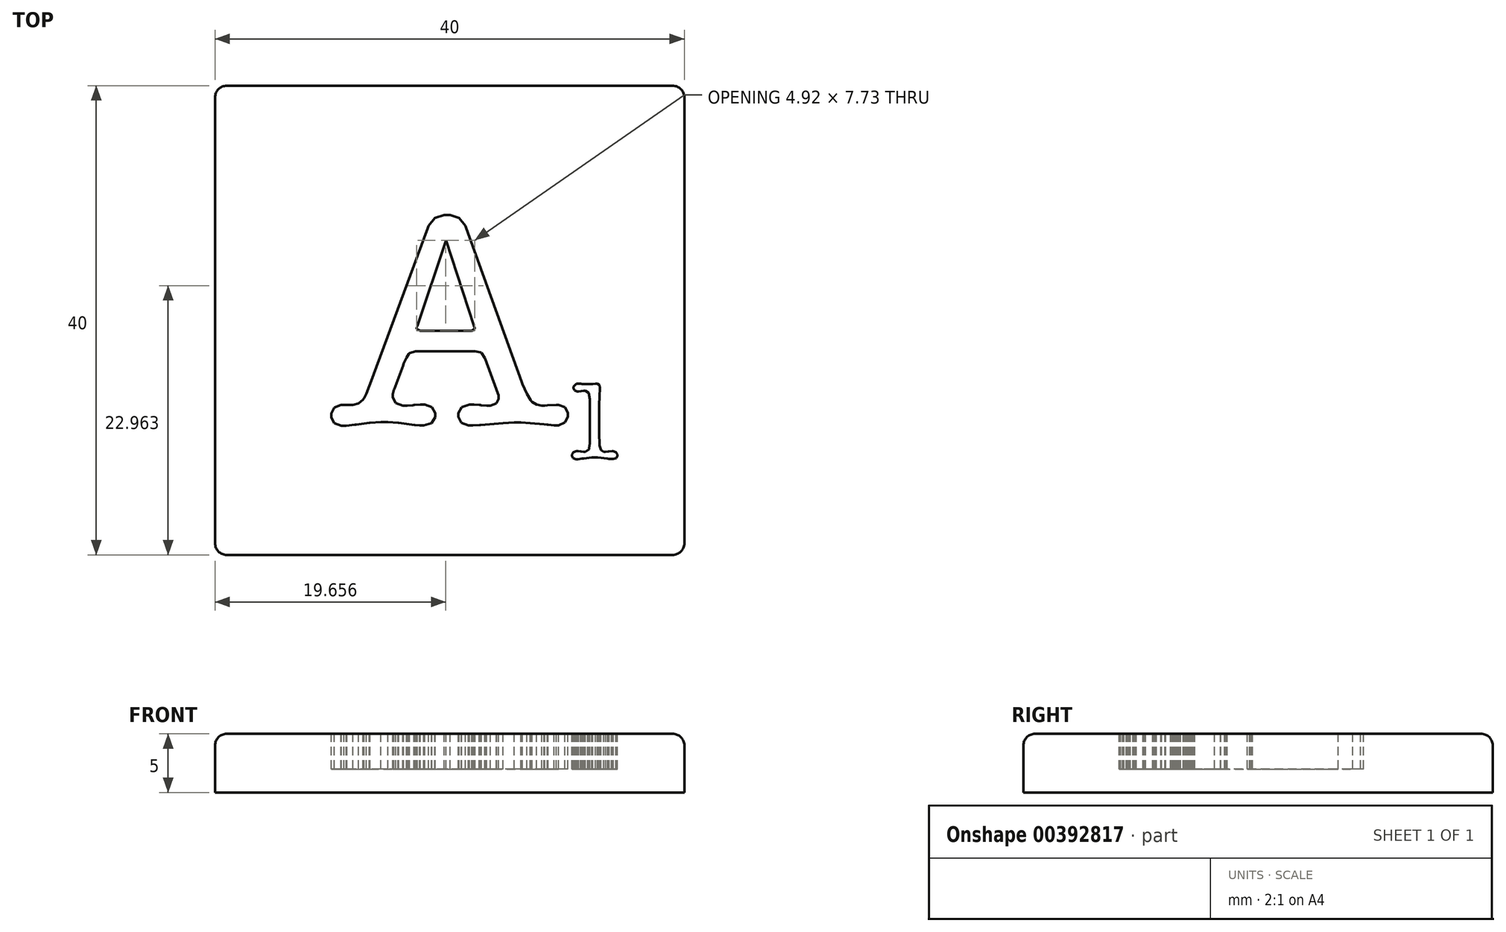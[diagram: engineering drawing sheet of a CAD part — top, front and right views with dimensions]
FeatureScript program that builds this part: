
annotation { "Feature Type Name" : "Feature", "Feature Type Description" : "" }
export const myFeature = defineFeature(function(context is Context, id is Id, definition is map)
    precondition{}
    {
        {
            var Q0;
            Q0=qCreatedBy(makeId("Top.planeOp"),FACE);
            var sketch = newSketch(context, id + "F0", { "sketchPlane" : qUnion([Q0])});
            skLineSegment(sketch, "E0.bottom", {"start": v(20, -20) * mm, "end": v(-20, -20) * mm});
            skLineSegment(sketch, "E0.top", {"start": v(20, 20) * mm, "end": v(-20, 20) * mm});
            skLineSegment(sketch, "E0.left", {"start": v(20, -20) * mm, "end": v(20, 20) * mm});
            skLineSegment(sketch, "E0.right", {"start": v(-20, -20) * mm, "end": v(-20, 20) * mm});
            skPoint(sketch, "E0.middle", {"position": v(0, 0) * mm});
            skSolve(sketch);
        }
        {
            var Q0;
            Q0=makeQuery(id+"F0.imprint","IMPRINT",FACE,{"disambiguationData":[TD([[makeQuery(id+"F0.imprint","IMPRINT",EDGE,{"derivedFrom":sQuery(id+"F0.wireOp",EDGE,"E0.bottom")}),-1.0]])]});
            extrude(context, id + "F1", {"entities" : qUnion([Q0]), "depth" : -5 * mm});
        }
        {
            var Q0;
            Q0=makeQuery(id+"F1.opExtrude","CAP_FACE",FACE,{"disambiguationData":[OSD([sQuery(id+"F0.wireOp",EDGE,"E0.bottom"),sQuery(id+"F0.wireOp",EDGE,"E0.top"),sQuery(id+"F0.wireOp",EDGE,"E0.left"),sQuery(id+"F0.wireOp",EDGE,"E0.right")])],"isStart":true});
            var Q1;
            Q1=makeQuery(id+"F1.opExtrude","SWEPT_EDGE",EDGE,{"disambiguationData":[OSD([sQuery(id+"F0.wireOp",EDGE,"E0.top"),sQuery(id+"F0.wireOp",EDGE,"E0.right")])]});
            var Q2;
            Q2=makeQuery(id+"F1.opExtrude","SWEPT_EDGE",EDGE,{"disambiguationData":[OSD([sQuery(id+"F0.wireOp",EDGE,"E0.top"),sQuery(id+"F0.wireOp",EDGE,"E0.left")])]});
            var Q3;
            Q3=makeQuery(id+"F1.opExtrude","SWEPT_EDGE",EDGE,{"disambiguationData":[OSD([sQuery(id+"F0.wireOp",EDGE,"E0.bottom"),sQuery(id+"F0.wireOp",EDGE,"E0.right")])]});
            var Q4;
            Q4=makeQuery(id+"F1.opExtrude","SWEPT_EDGE",EDGE,{"disambiguationData":[OSD([sQuery(id+"F0.wireOp",EDGE,"E0.bottom"),sQuery(id+"F0.wireOp",EDGE,"E0.left")])]});
            fillet(context, id + "F2", {"entities" : qUnion([Q0, Q1, Q2, Q3, Q4]), "radius" : 1 * mm, "tangentPropagation" : true, "allowEdgeOverflow" : false});
        }
        {
            var Q0;
            Q0=qCreatedBy(makeId("Top.planeOp"),FACE);
            var sketch = newSketch(context, id + "F3", { "sketchPlane" : qUnion([Q0])});
            skLineSegment(sketch, "E1", {"start": v(3.97, -5.87) * mm, "end": v(3.02, -3.28) * mm});
            skLineSegment(sketch, "E2", {"start": v(3.02, -3.28) * mm, "end": v(2.99, -3.2) * mm});
            skLineSegment(sketch, "E3", {"start": v(2.99, -3.2) * mm, "end": v(2.71, -2.77) * mm});
            skLineSegment(sketch, "E4", {"start": v(2.71, -2.77) * mm, "end": v(2.69, -2.75) * mm});
            skLineSegment(sketch, "E5", {"start": v(2.69, -2.75) * mm, "end": v(2.66, -2.73) * mm});
            skLineSegment(sketch, "E6", {"start": v(2.66, -2.73) * mm, "end": v(2.15, -2.65) * mm});
            skLineSegment(sketch, "E7", {"start": v(2.15, -2.65) * mm, "end": v(1.99, -2.65) * mm});
            skLineSegment(sketch, "E8", {"start": v(1.99, -2.65) * mm, "end": v(-2.73, -2.65) * mm});
            skLineSegment(sketch, "E9", {"start": v(-2.73, -2.65) * mm, "end": v(-2.9, -2.65) * mm});
            skLineSegment(sketch, "E10", {"start": v(-2.9, -2.65) * mm, "end": v(-3.42, -2.8) * mm});
            skLineSegment(sketch, "E11", {"start": v(-3.42, -2.8) * mm, "end": v(-3.45, -2.83) * mm});
            skLineSegment(sketch, "E12", {"start": v(-3.45, -2.83) * mm, "end": v(-3.49, -2.86) * mm});
            skLineSegment(sketch, "E13", {"start": v(-3.49, -2.86) * mm, "end": v(-3.68, -3.17) * mm});
            skLineSegment(sketch, "E14", {"start": v(-3.68, -3.17) * mm, "end": v(-3.92, -3.7) * mm});
            skLineSegment(sketch, "E15", {"start": v(-3.92, -3.7) * mm, "end": v(-3.97, -3.84) * mm});
            skLineSegment(sketch, "E16", {"start": v(-3.97, -3.84) * mm, "end": v(-4.74, -5.87) * mm});
            skLineSegment(sketch, "E17", {"start": v(-4.74, -5.87) * mm, "end": v(-4.75, -5.92) * mm});
            skLineSegment(sketch, "E18", {"start": v(-4.75, -5.92) * mm, "end": v(-4.84, -6.3) * mm});
            skLineSegment(sketch, "E19", {"start": v(-4.84, -6.3) * mm, "end": v(-4.84, -6.43) * mm});
            skLineSegment(sketch, "E20", {"start": v(-4.84, -6.43) * mm, "end": v(-4.84, -6.59) * mm});
            skLineSegment(sketch, "E21", {"start": v(-4.84, -6.59) * mm, "end": v(-4.58, -7.06) * mm});
            skLineSegment(sketch, "E22", {"start": v(-4.58, -7.06) * mm, "end": v(-4, -7.28) * mm});
            skLineSegment(sketch, "E23", {"start": v(-4, -7.28) * mm, "end": v(-3.8, -7.28) * mm});
            skLineSegment(sketch, "E24", {"start": v(-3.8, -7.28) * mm, "end": v(-3.62, -7.28) * mm});
            skLineSegment(sketch, "E25", {"start": v(-3.62, -7.28) * mm, "end": v(-3.14, -7.23) * mm});
            skLineSegment(sketch, "E26", {"start": v(-3.14, -7.23) * mm, "end": v(-3.06, -7.22) * mm});
            skLineSegment(sketch, "E27", {"start": v(-3.06, -7.22) * mm, "end": v(-2.97, -7.21) * mm});
            skLineSegment(sketch, "E28", {"start": v(-2.97, -7.21) * mm, "end": v(-2.5, -7.17) * mm});
            skLineSegment(sketch, "E29", {"start": v(-2.5, -7.17) * mm, "end": v(-2.33, -7.17) * mm});
            skLineSegment(sketch, "E30", {"start": v(-2.33, -7.17) * mm, "end": v(-2.13, -7.17) * mm});
            skLineSegment(sketch, "E31", {"start": v(-2.13, -7.17) * mm, "end": v(-1.52, -7.4) * mm});
            skLineSegment(sketch, "E32", {"start": v(-1.52, -7.4) * mm, "end": v(-1.24, -7.92) * mm});
            skLineSegment(sketch, "E33", {"start": v(-1.24, -7.92) * mm, "end": v(-1.24, -8.1) * mm});
            skLineSegment(sketch, "E34", {"start": v(-1.24, -8.1) * mm, "end": v(-1.24, -8.26) * mm});
            skLineSegment(sketch, "E35", {"start": v(-1.24, -8.26) * mm, "end": v(-1.54, -8.75) * mm});
            skLineSegment(sketch, "E36", {"start": v(-1.54, -8.75) * mm, "end": v(-2.21, -8.97) * mm});
            skLineSegment(sketch, "E37", {"start": v(-2.21, -8.97) * mm, "end": v(-2.43, -8.97) * mm});
            skLineSegment(sketch, "E38", {"start": v(-2.43, -8.97) * mm, "end": v(-2.58, -8.97) * mm});
            skLineSegment(sketch, "E39", {"start": v(-2.58, -8.97) * mm, "end": v(-2.96, -8.92) * mm});
            skLineSegment(sketch, "E40", {"start": v(-2.96, -8.92) * mm, "end": v(-3.02, -8.92) * mm});
            skLineSegment(sketch, "E41", {"start": v(-3.02, -8.92) * mm, "end": v(-4.34, -8.73) * mm});
            skLineSegment(sketch, "E42", {"start": v(-4.34, -8.73) * mm, "end": v(-4.4, -8.72) * mm});
            skLineSegment(sketch, "E43", {"start": v(-4.4, -8.72) * mm, "end": v(-5.27, -8.68) * mm});
            skLineSegment(sketch, "E44", {"start": v(-5.27, -8.68) * mm, "end": v(-5.56, -8.68) * mm});
            skLineSegment(sketch, "E45", {"start": v(-5.56, -8.68) * mm, "end": v(-5.88, -8.68) * mm});
            skLineSegment(sketch, "E46", {"start": v(-5.88, -8.68) * mm, "end": v(-6.8, -8.72) * mm});
            skLineSegment(sketch, "E47", {"start": v(-6.8, -8.72) * mm, "end": v(-6.85, -8.73) * mm});
            skLineSegment(sketch, "E48", {"start": v(-6.85, -8.73) * mm, "end": v(-7.96, -8.89) * mm});
            skLineSegment(sketch, "E49", {"start": v(-7.96, -8.89) * mm, "end": v(-8.09, -8.9) * mm});
            skLineSegment(sketch, "E50", {"start": v(-8.09, -8.9) * mm, "end": v(-8.8, -9) * mm});
            skLineSegment(sketch, "E51", {"start": v(-8.8, -9) * mm, "end": v(-9.05, -9) * mm});
            skLineSegment(sketch, "E52", {"start": v(-9.05, -9) * mm, "end": v(-9.24, -9) * mm});
            skLineSegment(sketch, "E53", {"start": v(-9.24, -9) * mm, "end": v(-9.82, -8.78) * mm});
            skLineSegment(sketch, "E54", {"start": v(-9.82, -8.78) * mm, "end": v(-10.08, -8.28) * mm});
            skLineSegment(sketch, "E55", {"start": v(-10.08, -8.28) * mm, "end": v(-10.08, -8.12) * mm});
            skLineSegment(sketch, "E56", {"start": v(-10.08, -8.12) * mm, "end": v(-10.08, -7.95) * mm});
            skLineSegment(sketch, "E57", {"start": v(-10.08, -7.95) * mm, "end": v(-9.83, -7.43) * mm});
            skLineSegment(sketch, "E58", {"start": v(-9.83, -7.43) * mm, "end": v(-9.26, -7.2) * mm});
            skLineSegment(sketch, "E59", {"start": v(-9.26, -7.2) * mm, "end": v(-9.08, -7.2) * mm});
            skLineSegment(sketch, "E60", {"start": v(-9.08, -7.2) * mm, "end": v(-9, -7.2) * mm});
            skLineSegment(sketch, "E61", {"start": v(-9, -7.2) * mm, "end": v(-8.78, -7.22) * mm});
            skLineSegment(sketch, "E62", {"start": v(-8.78, -7.22) * mm, "end": v(-8.76, -7.22) * mm});
            skLineSegment(sketch, "E63", {"start": v(-8.76, -7.22) * mm, "end": v(-8.41, -7.22) * mm});
            skLineSegment(sketch, "E64", {"start": v(-8.41, -7.22) * mm, "end": v(-8.26, -7.22) * mm});
            skLineSegment(sketch, "E65", {"start": v(-8.26, -7.22) * mm, "end": v(-7.79, -7.08) * mm});
            skLineSegment(sketch, "E66", {"start": v(-7.79, -7.08) * mm, "end": v(-7.4, -6.76) * mm});
            skLineSegment(sketch, "E67", {"start": v(-7.4, -6.76) * mm, "end": v(-7.33, -6.67) * mm});
            skLineSegment(sketch, "E68", {"start": v(-7.33, -6.67) * mm, "end": v(-7.3, -6.63) * mm});
            skLineSegment(sketch, "E69", {"start": v(-7.3, -6.63) * mm, "end": v(-7.12, -6.25) * mm});
            skLineSegment(sketch, "E70", {"start": v(-7.12, -6.25) * mm, "end": v(-6.86, -5.6) * mm});
            skLineSegment(sketch, "E71", {"start": v(-6.86, -5.6) * mm, "end": v(-6.8, -5.42) * mm});
            skLineSegment(sketch, "E72", {"start": v(-6.8, -5.42) * mm, "end": v(-1.88, 7.89) * mm});
            skLineSegment(sketch, "E73", {"start": v(-1.88, 7.89) * mm, "end": v(-1.8, 8.07) * mm});
            skLineSegment(sketch, "E74", {"start": v(-1.8, 8.07) * mm, "end": v(-1.25, 8.72) * mm});
            skLineSegment(sketch, "E75", {"start": v(-1.25, 8.72) * mm, "end": v(-0.47, 9) * mm});
            skLineSegment(sketch, "E76", {"start": v(-0.47, 9) * mm, "end": v(-0.21, 9) * mm});
            skLineSegment(sketch, "E77", {"start": v(-0.21, 9) * mm, "end": v(0.04, 9) * mm});
            skLineSegment(sketch, "E78", {"start": v(0.04, 9) * mm, "end": v(0.8, 8.72) * mm});
            skLineSegment(sketch, "E79", {"start": v(0.8, 8.72) * mm, "end": v(1.34, 8.07) * mm});
            skLineSegment(sketch, "E80", {"start": v(1.34, 8.07) * mm, "end": v(1.4, 7.89) * mm});
            skLineSegment(sketch, "E81", {"start": v(1.4, 7.89) * mm, "end": v(6.14, -5.24) * mm});
            skLineSegment(sketch, "E82", {"start": v(6.14, -5.24) * mm, "end": v(6.21, -5.45) * mm});
            skLineSegment(sketch, "E83", {"start": v(6.21, -5.45) * mm, "end": v(6.57, -6.27) * mm});
            skLineSegment(sketch, "E84", {"start": v(6.57, -6.27) * mm, "end": v(6.9, -6.81) * mm});
            skLineSegment(sketch, "E85", {"start": v(6.9, -6.81) * mm, "end": v(6.96, -6.88) * mm});
            skLineSegment(sketch, "E86", {"start": v(6.96, -6.88) * mm, "end": v(7.02, -6.95) * mm});
            skLineSegment(sketch, "E87", {"start": v(7.02, -6.95) * mm, "end": v(7.4, -7.18) * mm});
            skLineSegment(sketch, "E88", {"start": v(7.4, -7.18) * mm, "end": v(7.86, -7.28) * mm});
            skLineSegment(sketch, "E89", {"start": v(7.86, -7.28) * mm, "end": v(8.02, -7.28) * mm});
            skLineSegment(sketch, "E90", {"start": v(8.02, -7.28) * mm, "end": v(8.1, -7.28) * mm});
            skLineSegment(sketch, "E91", {"start": v(8.1, -7.28) * mm, "end": v(8.32, -7.25) * mm});
            skLineSegment(sketch, "E92", {"start": v(8.32, -7.25) * mm, "end": v(8.34, -7.25) * mm});
            skLineSegment(sketch, "E93", {"start": v(8.34, -7.25) * mm, "end": v(9.08, -7.2) * mm});
            skLineSegment(sketch, "E94", {"start": v(9.08, -7.2) * mm, "end": v(9.26, -7.2) * mm});
            skLineSegment(sketch, "E95", {"start": v(9.26, -7.2) * mm, "end": v(9.83, -7.4) * mm});
            skLineSegment(sketch, "E96", {"start": v(9.83, -7.4) * mm, "end": v(10.08, -7.88) * mm});
            skLineSegment(sketch, "E97", {"start": v(10.08, -7.88) * mm, "end": v(10.08, -8.04) * mm});
            skLineSegment(sketch, "E98", {"start": v(10.08, -8.04) * mm, "end": v(10.08, -8.21) * mm});
            skLineSegment(sketch, "E99", {"start": v(10.08, -8.21) * mm, "end": v(9.83, -8.72) * mm});
            skLineSegment(sketch, "E100", {"start": v(9.83, -8.72) * mm, "end": v(9.26, -8.94) * mm});
            skLineSegment(sketch, "E101", {"start": v(9.26, -8.94) * mm, "end": v(9.08, -8.94) * mm});
            skLineSegment(sketch, "E102", {"start": v(9.08, -8.94) * mm, "end": v(8.88, -8.94) * mm});
            skLineSegment(sketch, "E103", {"start": v(8.88, -8.94) * mm, "end": v(8.39, -8.9) * mm});
            skLineSegment(sketch, "E104", {"start": v(8.39, -8.9) * mm, "end": v(8.3, -8.89) * mm});
            skLineSegment(sketch, "E105", {"start": v(8.3, -8.89) * mm, "end": v(8.03, -8.86) * mm});
            skLineSegment(sketch, "E106", {"start": v(8.03, -8.86) * mm, "end": v(6.85, -8.75) * mm});
            skLineSegment(sketch, "E107", {"start": v(6.85, -8.75) * mm, "end": v(6.08, -8.7) * mm});
            skLineSegment(sketch, "E108", {"start": v(6.08, -8.7) * mm, "end": v(5.82, -8.7) * mm});
            skLineSegment(sketch, "E109", {"start": v(5.82, -8.7) * mm, "end": v(5.5, -8.7) * mm});
            skLineSegment(sketch, "E110", {"start": v(5.5, -8.7) * mm, "end": v(4.54, -8.76) * mm});
            skLineSegment(sketch, "E111", {"start": v(4.54, -8.76) * mm, "end": v(3.01, -8.88) * mm});
            skLineSegment(sketch, "E112", {"start": v(3.01, -8.88) * mm, "end": v(2.65, -8.92) * mm});
            skLineSegment(sketch, "E113", {"start": v(2.65, -8.92) * mm, "end": v(2.55, -8.92) * mm});
            skLineSegment(sketch, "E114", {"start": v(2.55, -8.92) * mm, "end": v(1.99, -8.97) * mm});
            skLineSegment(sketch, "E115", {"start": v(1.99, -8.97) * mm, "end": v(1.8, -8.97) * mm});
            skLineSegment(sketch, "E116", {"start": v(1.8, -8.97) * mm, "end": v(1.6, -8.97) * mm});
            skLineSegment(sketch, "E117", {"start": v(1.6, -8.97) * mm, "end": v(1, -8.74) * mm});
            skLineSegment(sketch, "E118", {"start": v(1, -8.74) * mm, "end": v(0.74, -8.24) * mm});
            skLineSegment(sketch, "E119", {"start": v(0.74, -8.24) * mm, "end": v(0.74, -8.07) * mm});
            skLineSegment(sketch, "E120", {"start": v(0.74, -8.07) * mm, "end": v(0.74, -7.9) * mm});
            skLineSegment(sketch, "E121", {"start": v(0.74, -7.9) * mm, "end": v(1.03, -7.4) * mm});
            skLineSegment(sketch, "E122", {"start": v(1.03, -7.4) * mm, "end": v(1.69, -7.17) * mm});
            skLineSegment(sketch, "E123", {"start": v(1.69, -7.17) * mm, "end": v(1.9, -7.17) * mm});
            skLineSegment(sketch, "E124", {"start": v(1.9, -7.17) * mm, "end": v(2.08, -7.17) * mm});
            skLineSegment(sketch, "E125", {"start": v(2.08, -7.17) * mm, "end": v(2.53, -7.21) * mm});
            skLineSegment(sketch, "E126", {"start": v(2.53, -7.21) * mm, "end": v(2.6, -7.22) * mm});
            skLineSegment(sketch, "E127", {"start": v(2.6, -7.22) * mm, "end": v(2.68, -7.23) * mm});
            skLineSegment(sketch, "E128", {"start": v(2.68, -7.23) * mm, "end": v(3.15, -7.28) * mm});
            skLineSegment(sketch, "E129", {"start": v(3.15, -7.28) * mm, "end": v(3.3, -7.28) * mm});
            skLineSegment(sketch, "E130", {"start": v(3.3, -7.28) * mm, "end": v(3.47, -7.28) * mm});
            skLineSegment(sketch, "E131", {"start": v(3.47, -7.28) * mm, "end": v(3.96, -7.1) * mm});
            skLineSegment(sketch, "E132", {"start": v(3.96, -7.1) * mm, "end": v(4.18, -6.7) * mm});
            skLineSegment(sketch, "E133", {"start": v(4.18, -6.7) * mm, "end": v(4.18, -6.56) * mm});
            skLineSegment(sketch, "E134", {"start": v(4.18, -6.56) * mm, "end": v(4.18, -6.39) * mm});
            skLineSegment(sketch, "E135", {"start": v(4.18, -6.39) * mm, "end": v(4, -5.97) * mm});
            skLineSegment(sketch, "E136", {"start": v(4, -5.97) * mm, "end": v(3.97, -5.87) * mm});
            skLineSegment(sketch, "E137", {"start": v(2.06, -0.48) * mm, "end": v(-0.32, 6.83) * mm});
            skLineSegment(sketch, "E138", {"start": v(-0.32, 6.83) * mm, "end": v(-2.75, -0.48) * mm});
            skLineSegment(sketch, "E139", {"start": v(-2.75, -0.48) * mm, "end": v(-2.76, -0.5) * mm});
            skLineSegment(sketch, "E140", {"start": v(-2.76, -0.5) * mm, "end": v(-2.8, -0.62) * mm});
            skLineSegment(sketch, "E141", {"start": v(-2.8, -0.62) * mm, "end": v(-2.8, -0.66) * mm});
            skLineSegment(sketch, "E142", {"start": v(-2.8, -0.66) * mm, "end": v(-2.8, -0.72) * mm});
            skLineSegment(sketch, "E143", {"start": v(-2.8, -0.72) * mm, "end": v(-2.5, -0.9) * mm});
            skLineSegment(sketch, "E144", {"start": v(-2.5, -0.9) * mm, "end": v(-2.4, -0.9) * mm});
            skLineSegment(sketch, "E145", {"start": v(-2.4, -0.9) * mm, "end": v(1.8, -0.9) * mm});
            skLineSegment(sketch, "E146", {"start": v(1.8, -0.9) * mm, "end": v(1.88, -0.9) * mm});
            skLineSegment(sketch, "E147", {"start": v(1.88, -0.9) * mm, "end": v(2.12, -0.74) * mm});
            skLineSegment(sketch, "E148", {"start": v(2.12, -0.74) * mm, "end": v(2.12, -0.69) * mm});
            skLineSegment(sketch, "E149", {"start": v(2.12, -0.69) * mm, "end": v(2.12, -0.63) * mm});
            skLineSegment(sketch, "E150", {"start": v(2.12, -0.63) * mm, "end": v(2.07, -0.5) * mm});
            skLineSegment(sketch, "E151", {"start": v(2.07, -0.5) * mm, "end": v(2.06, -0.48) * mm});
            skSolve(sketch);
        }
        {
            var Q0;
            Q0=qCreatedBy(makeId("Top.planeOp"),FACE);
            var sketch = newSketch(context, id + "F4", { "sketchPlane" : qUnion([Q0])});
            skLineSegment(sketch, "E152", {"start": v(11.96, -9.59) * mm, "end": v(11.93, -6.82) * mm});
            skLineSegment(sketch, "E153", {"start": v(11.93, -6.82) * mm, "end": v(11.93, -6.74) * mm});
            skLineSegment(sketch, "E154", {"start": v(11.93, -6.74) * mm, "end": v(11.85, -6.2) * mm});
            skLineSegment(sketch, "E155", {"start": v(11.85, -6.2) * mm, "end": v(11.83, -6.18) * mm});
            skLineSegment(sketch, "E156", {"start": v(11.83, -6.18) * mm, "end": v(11.82, -6.15) * mm});
            skLineSegment(sketch, "E157", {"start": v(11.82, -6.15) * mm, "end": v(11.56, -6.01) * mm});
            skLineSegment(sketch, "E158", {"start": v(11.56, -6.01) * mm, "end": v(11.47, -6.01) * mm});
            skLineSegment(sketch, "E159", {"start": v(11.47, -6.01) * mm, "end": v(11.4, -6.01) * mm});
            skLineSegment(sketch, "E160", {"start": v(11.4, -6.01) * mm, "end": v(11.23, -6.03) * mm});
            skLineSegment(sketch, "E161", {"start": v(11.23, -6.03) * mm, "end": v(11.2, -6.04) * mm});
            skLineSegment(sketch, "E162", {"start": v(11.2, -6.04) * mm, "end": v(11.17, -6.04) * mm});
            skLineSegment(sketch, "E163", {"start": v(11.17, -6.04) * mm, "end": v(10.98, -6.06) * mm});
            skLineSegment(sketch, "E164", {"start": v(10.98, -6.06) * mm, "end": v(10.92, -6.06) * mm});
            skLineSegment(sketch, "E165", {"start": v(10.92, -6.06) * mm, "end": v(10.85, -6.06) * mm});
            skLineSegment(sketch, "E166", {"start": v(10.85, -6.06) * mm, "end": v(10.64, -5.98) * mm});
            skLineSegment(sketch, "E167", {"start": v(10.64, -5.98) * mm, "end": v(10.55, -5.79) * mm});
            skLineSegment(sketch, "E168", {"start": v(10.55, -5.79) * mm, "end": v(10.55, -5.73) * mm});
            skLineSegment(sketch, "E169", {"start": v(10.55, -5.73) * mm, "end": v(10.55, -5.64) * mm});
            skLineSegment(sketch, "E170", {"start": v(10.55, -5.64) * mm, "end": v(10.81, -5.4) * mm});
            skLineSegment(sketch, "E171", {"start": v(10.81, -5.4) * mm, "end": v(10.9, -5.4) * mm});
            skLineSegment(sketch, "E172", {"start": v(10.9, -5.4) * mm, "end": v(11, -5.4) * mm});
            skLineSegment(sketch, "E173", {"start": v(11, -5.4) * mm, "end": v(11.22, -5.41) * mm});
            skLineSegment(sketch, "E174", {"start": v(11.22, -5.41) * mm, "end": v(11.26, -5.42) * mm});
            skLineSegment(sketch, "E175", {"start": v(11.26, -5.42) * mm, "end": v(11.3, -5.42) * mm});
            skLineSegment(sketch, "E176", {"start": v(11.3, -5.42) * mm, "end": v(11.55, -5.44) * mm});
            skLineSegment(sketch, "E177", {"start": v(11.55, -5.44) * mm, "end": v(11.64, -5.44) * mm});
            skLineSegment(sketch, "E178", {"start": v(11.64, -5.44) * mm, "end": v(11.76, -5.44) * mm});
            skLineSegment(sketch, "E179", {"start": v(11.76, -5.44) * mm, "end": v(12.1, -5.43) * mm});
            skLineSegment(sketch, "E180", {"start": v(12.1, -5.43) * mm, "end": v(12.14, -5.42) * mm});
            skLineSegment(sketch, "E181", {"start": v(12.14, -5.42) * mm, "end": v(12.19, -5.42) * mm});
            skLineSegment(sketch, "E182", {"start": v(12.19, -5.42) * mm, "end": v(12.42, -5.4) * mm});
            skLineSegment(sketch, "E183", {"start": v(12.42, -5.4) * mm, "end": v(12.5, -5.4) * mm});
            skLineSegment(sketch, "E184", {"start": v(12.5, -5.4) * mm, "end": v(12.57, -5.4) * mm});
            skLineSegment(sketch, "E185", {"start": v(12.57, -5.4) * mm, "end": v(12.75, -5.5) * mm});
            skLineSegment(sketch, "E186", {"start": v(12.75, -5.5) * mm, "end": v(12.76, -5.52) * mm});
            skLineSegment(sketch, "E187", {"start": v(12.76, -5.52) * mm, "end": v(12.77, -5.53) * mm});
            skLineSegment(sketch, "E188", {"start": v(12.77, -5.53) * mm, "end": v(12.8, -5.74) * mm});
            skLineSegment(sketch, "E189", {"start": v(12.8, -5.74) * mm, "end": v(12.8, -5.81) * mm});
            skLineSegment(sketch, "E190", {"start": v(12.8, -5.81) * mm, "end": v(12.8, -5.87) * mm});
            skLineSegment(sketch, "E191", {"start": v(12.8, -5.87) * mm, "end": v(12.79, -6) * mm});
            skLineSegment(sketch, "E192", {"start": v(12.79, -6) * mm, "end": v(12.79, -6.04) * mm});
            skLineSegment(sketch, "E193", {"start": v(12.79, -6.04) * mm, "end": v(12.78, -6.21) * mm});
            skLineSegment(sketch, "E194", {"start": v(12.78, -6.21) * mm, "end": v(12.74, -7.47) * mm});
            skLineSegment(sketch, "E195", {"start": v(12.74, -7.47) * mm, "end": v(12.74, -7.9) * mm});
            skLineSegment(sketch, "E196", {"start": v(12.74, -7.9) * mm, "end": v(12.74, -8.97) * mm});
            skLineSegment(sketch, "E197", {"start": v(12.74, -8.97) * mm, "end": v(12.75, -9.67) * mm});
            skLineSegment(sketch, "E198", {"start": v(12.75, -9.67) * mm, "end": v(12.75, -9.76) * mm});
            skLineSegment(sketch, "E199", {"start": v(12.75, -9.76) * mm, "end": v(12.75, -9.86) * mm});
            skLineSegment(sketch, "E200", {"start": v(12.75, -9.86) * mm, "end": v(12.77, -10.37) * mm});
            skLineSegment(sketch, "E201", {"start": v(12.77, -10.37) * mm, "end": v(12.77, -10.55) * mm});
            skLineSegment(sketch, "E202", {"start": v(12.77, -10.55) * mm, "end": v(12.77, -10.66) * mm});
            skLineSegment(sketch, "E203", {"start": v(12.77, -10.66) * mm, "end": v(12.88, -11.04) * mm});
            skLineSegment(sketch, "E204", {"start": v(12.88, -11.04) * mm, "end": v(13.13, -11.2) * mm});
            skLineSegment(sketch, "E205", {"start": v(13.13, -11.2) * mm, "end": v(13.2, -11.2) * mm});
            skLineSegment(sketch, "E206", {"start": v(13.2, -11.2) * mm, "end": v(13.29, -11.2) * mm});
            skLineSegment(sketch, "E207", {"start": v(13.29, -11.2) * mm, "end": v(13.49, -11.18) * mm});
            skLineSegment(sketch, "E208", {"start": v(13.49, -11.18) * mm, "end": v(13.52, -11.18) * mm});
            skLineSegment(sketch, "E209", {"start": v(13.52, -11.18) * mm, "end": v(13.56, -11.18) * mm});
            skLineSegment(sketch, "E210", {"start": v(13.56, -11.18) * mm, "end": v(13.84, -11.16) * mm});
            skLineSegment(sketch, "E211", {"start": v(13.84, -11.16) * mm, "end": v(13.92, -11.16) * mm});
            skLineSegment(sketch, "E212", {"start": v(13.92, -11.16) * mm, "end": v(14.18, -11.24) * mm});
            skLineSegment(sketch, "E213", {"start": v(14.18, -11.24) * mm, "end": v(14.3, -11.43) * mm});
            skLineSegment(sketch, "E214", {"start": v(14.3, -11.43) * mm, "end": v(14.3, -11.5) * mm});
            skLineSegment(sketch, "E215", {"start": v(14.3, -11.5) * mm, "end": v(14.3, -11.55) * mm});
            skLineSegment(sketch, "E216", {"start": v(14.3, -11.55) * mm, "end": v(14.19, -11.74) * mm});
            skLineSegment(sketch, "E217", {"start": v(14.19, -11.74) * mm, "end": v(13.95, -11.82) * mm});
            skLineSegment(sketch, "E218", {"start": v(13.95, -11.82) * mm, "end": v(13.87, -11.82) * mm});
            skLineSegment(sketch, "E219", {"start": v(13.87, -11.82) * mm, "end": v(13.8, -11.82) * mm});
            skLineSegment(sketch, "E220", {"start": v(13.8, -11.82) * mm, "end": v(13.6, -11.8) * mm});
            skLineSegment(sketch, "E221", {"start": v(13.6, -11.8) * mm, "end": v(13.57, -11.8) * mm});
            skLineSegment(sketch, "E222", {"start": v(13.57, -11.8) * mm, "end": v(13.44, -11.79) * mm});
            skLineSegment(sketch, "E223", {"start": v(13.44, -11.79) * mm, "end": v(12.62, -11.7) * mm});
            skLineSegment(sketch, "E224", {"start": v(12.62, -11.7) * mm, "end": v(12.35, -11.7) * mm});
            skLineSegment(sketch, "E225", {"start": v(12.35, -11.7) * mm, "end": v(12.1, -11.7) * mm});
            skLineSegment(sketch, "E226", {"start": v(12.1, -11.7) * mm, "end": v(11.42, -11.77) * mm});
            skLineSegment(sketch, "E227", {"start": v(11.42, -11.77) * mm, "end": v(11.32, -11.79) * mm});
            skLineSegment(sketch, "E228", {"start": v(11.32, -11.79) * mm, "end": v(11.26, -11.8) * mm});
            skLineSegment(sketch, "E229", {"start": v(11.26, -11.8) * mm, "end": v(10.94, -11.83) * mm});
            skLineSegment(sketch, "E230", {"start": v(10.94, -11.83) * mm, "end": v(10.83, -11.83) * mm});
            skLineSegment(sketch, "E231", {"start": v(10.83, -11.83) * mm, "end": v(10.76, -11.83) * mm});
            skLineSegment(sketch, "E232", {"start": v(10.76, -11.83) * mm, "end": v(10.53, -11.75) * mm});
            skLineSegment(sketch, "E233", {"start": v(10.53, -11.75) * mm, "end": v(10.43, -11.55) * mm});
            skLineSegment(sketch, "E234", {"start": v(10.43, -11.55) * mm, "end": v(10.43, -11.5) * mm});
            skLineSegment(sketch, "E235", {"start": v(10.43, -11.5) * mm, "end": v(10.43, -11.43) * mm});
            skLineSegment(sketch, "E236", {"start": v(10.43, -11.43) * mm, "end": v(10.54, -11.24) * mm});
            skLineSegment(sketch, "E237", {"start": v(10.54, -11.24) * mm, "end": v(10.8, -11.16) * mm});
            skLineSegment(sketch, "E238", {"start": v(10.8, -11.16) * mm, "end": v(10.9, -11.16) * mm});
            skLineSegment(sketch, "E239", {"start": v(10.9, -11.16) * mm, "end": v(10.97, -11.16) * mm});
            skLineSegment(sketch, "E240", {"start": v(10.97, -11.16) * mm, "end": v(11.16, -11.18) * mm});
            skLineSegment(sketch, "E241", {"start": v(11.16, -11.18) * mm, "end": v(11.19, -11.19) * mm});
            skLineSegment(sketch, "E242", {"start": v(11.19, -11.19) * mm, "end": v(11.22, -11.19) * mm});
            skLineSegment(sketch, "E243", {"start": v(11.22, -11.19) * mm, "end": v(11.41, -11.2) * mm});
            skLineSegment(sketch, "E244", {"start": v(11.41, -11.2) * mm, "end": v(11.47, -11.2) * mm});
            skLineSegment(sketch, "E245", {"start": v(11.47, -11.2) * mm, "end": v(11.58, -11.2) * mm});
            skLineSegment(sketch, "E246", {"start": v(11.58, -11.2) * mm, "end": v(11.87, -10.99) * mm});
            skLineSegment(sketch, "E247", {"start": v(11.87, -10.99) * mm, "end": v(11.88, -10.94) * mm});
            skLineSegment(sketch, "E248", {"start": v(11.88, -10.94) * mm, "end": v(11.9, -10.9) * mm});
            skLineSegment(sketch, "E249", {"start": v(11.9, -10.9) * mm, "end": v(11.94, -10.47) * mm});
            skLineSegment(sketch, "E250", {"start": v(11.94, -10.47) * mm, "end": v(11.96, -9.8) * mm});
            skLineSegment(sketch, "E251", {"start": v(11.96, -9.8) * mm, "end": v(11.96, -9.59) * mm});
            skSolve(sketch);
        }
        {
            var Q0;
            Q0 = qSketchRegion(id + "F4", true);
            var Q1;
            Q1 = qSketchRegion(id + "F3", true);
            extrude(context, id + "F5", {"entities" : qUnion([Q0, Q1]), "depth" : -3 * mm});
        }
    });
